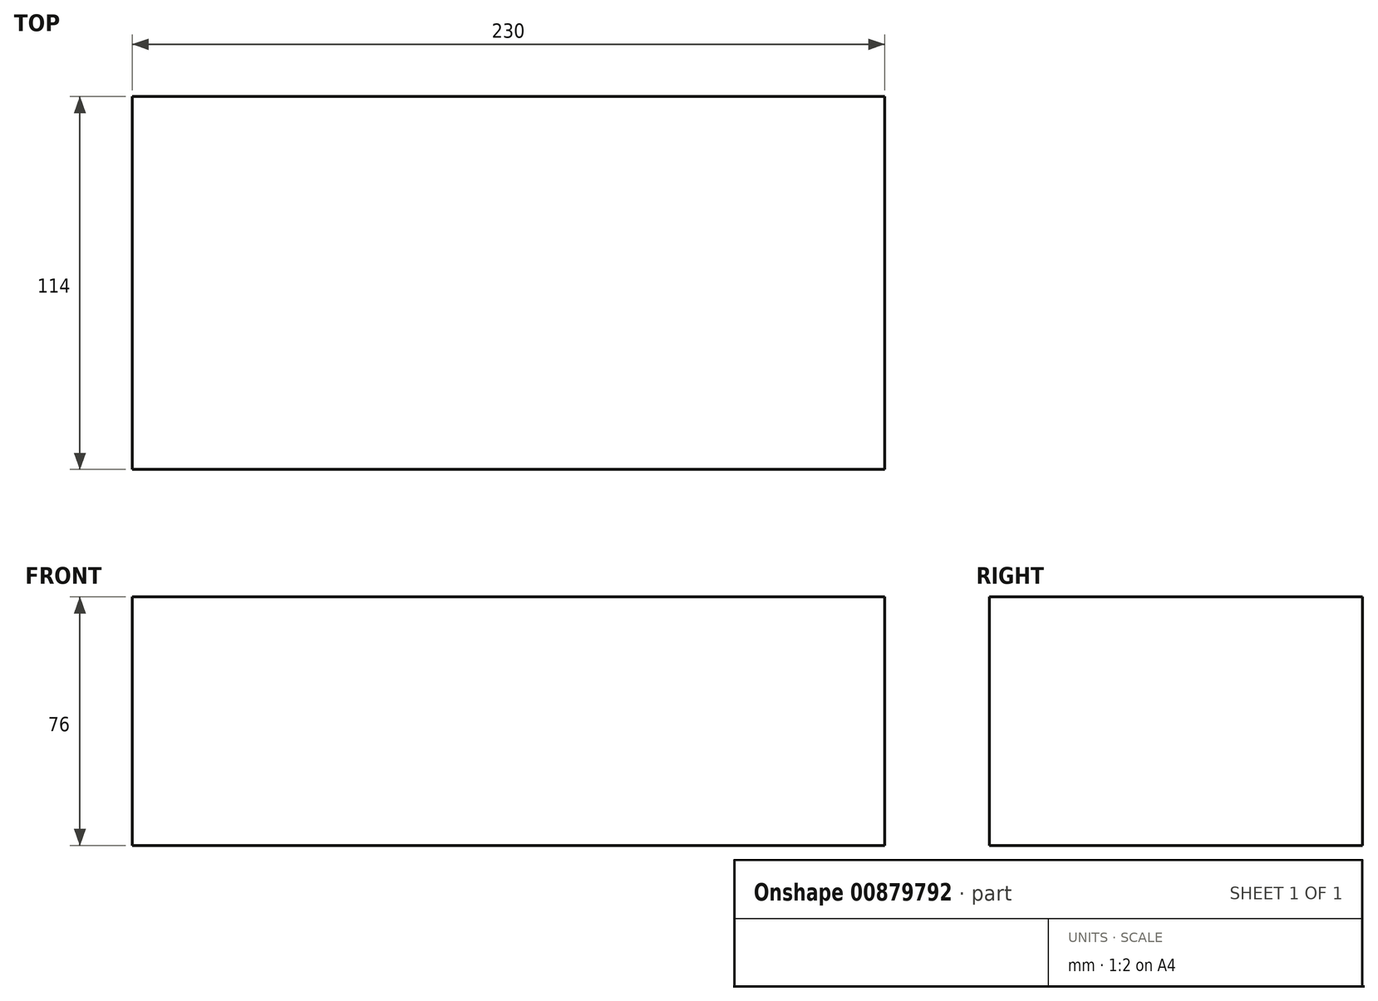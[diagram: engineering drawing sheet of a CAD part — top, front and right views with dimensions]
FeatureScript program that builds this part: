
annotation { "Feature Type Name" : "Feature", "Feature Type Description" : "" }
export const myFeature = defineFeature(function(context is Context, id is Id, definition is map)
    precondition{}
    {
        {
            var Q0;
            Q0=qCreatedBy(makeId("Top.planeOp"),FACE);
            var sketch = newSketch(context, id + "F0", { "sketchPlane" : qUnion([Q0])});
            skLineSegment(sketch, "E0", {"start": v(0, 0) * mm, "end": v(-115, 0) * mm, "construction": true});
            skLineSegment(sketch, "E1", {"start": v(-115, 0) * mm, "end": v(-115, -57) * mm, "construction": true});
            skLineSegment(sketch, "E2.bottom", {"start": v(-115, -57) * mm, "end": v(115, -57) * mm});
            skLineSegment(sketch, "E2.top", {"start": v(-115, 57) * mm, "end": v(115, 57) * mm});
            skLineSegment(sketch, "E2.left", {"start": v(-115, -57) * mm, "end": v(-115, 57) * mm});
            skLineSegment(sketch, "E2.right", {"start": v(115, -57) * mm, "end": v(115, 57) * mm});
            skSolve(sketch);
        }
        {
            var Q0;
            Q0=makeQuery(id+"F0.imprint","IMPRINT",FACE,{"disambiguationData":[TD([[makeQuery(id+"F0.imprint","IMPRINT",EDGE,{"derivedFrom":sQuery(id+"F0.wireOp",EDGE,"E2.bottom")}),1.0]])]});
            extrude(context, id + "F1", {"entities" : qUnion([Q0]), "depth" : 76 * mm, "offsetDistance" : 25 * mm, "symmetric" : true});
        }
    });
